# Revit family: 56117 Aquarius Universal 5000
name_source: partatom
category: Körper
revit_build: Autodesk Revit 2015 (Build: 20140606_1530(x64)
units: mm (PartAtom-declared; Revit-internal decimal feet)

## types (1)
- Aquarius Universal 5000
    Beschreibung = controllable pump via DMX/RDM
    Connection for hoses = 1, 1 1/4 , 1 1/2 inch
    Dimensionsincl incl. filter LxWxH = 315x140x130
    Electronic adjustment = yes
    Environmeantal condition submersible application = Water temperature min -20 °C to max. 35°C
    Filter housing = Plastic / stainless steel 1.4301 (AISI 304)
    Filter surface = 200 cm²
    Hersteller = OASE GmbH Post Box 2069, 48469 Hörstel , Germany +49 5454 80-0
    Homepage = http://www.oase-livingwater.com
    Immersion depth max. = 4 m
    Max. Flow rate = 83 l/min
    Max. flow rate = 5000 l/h
    Max. head height = 4.5 m
    Modell = Aquarius Universal 5000
    Power cable length = 10 m
    Power consumption = 85 W
    Pressure side connection = 1  inch
    Pump housing = Plastic
    Rated voltage = 220-240/50 V/Hz
    Suction side connection = 1 1/2  inch
    Weight = 3.42 kg
    installation = wet or dry
    oder no. = 56617

## geometry (parser evidence)
native form markers: Blend x6
no freeform markers — native parametric forms only
